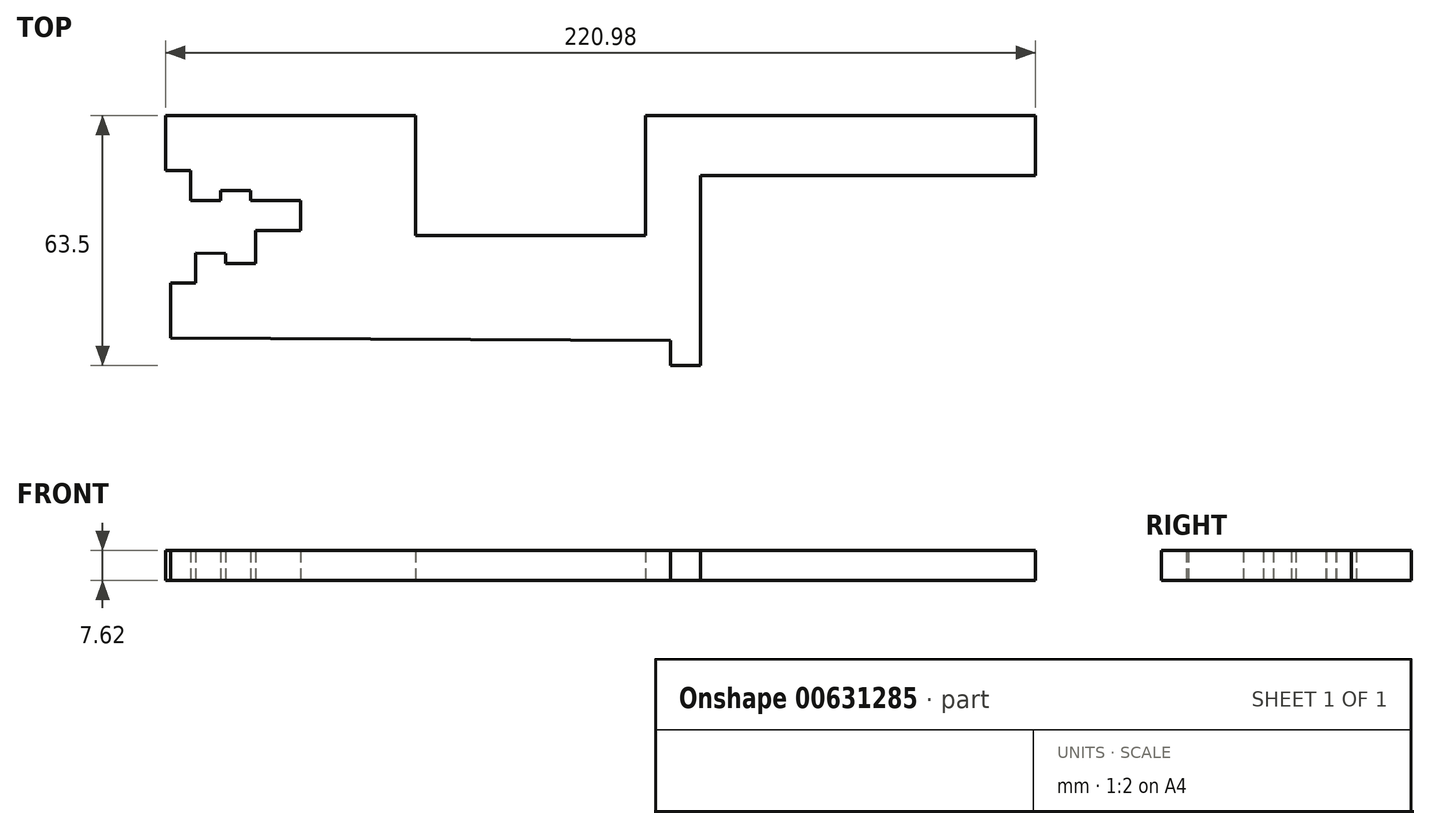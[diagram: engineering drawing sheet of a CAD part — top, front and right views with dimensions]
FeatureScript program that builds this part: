
annotation { "Feature Type Name" : "Feature", "Feature Type Description" : "" }
export const myFeature = defineFeature(function(context is Context, id is Id, definition is map)
    precondition{}
    {
        {
            var Q0;
            Q0=qCreatedBy(makeId("Top.planeOp"),FACE);
            var sketch = newSketch(context, id + "F0", { "sketchPlane" : qUnion([Q0])});
            skLineSegment(sketch, "E0", {"start": v(-135.89, 56.59) * mm, "end": v(-72.39, 56.59) * mm});
            skLineSegment(sketch, "E1", {"start": v(-72.39, 56.59) * mm, "end": v(-72.39, 26.1) * mm});
            skLineSegment(sketch, "E2", {"start": v(-72.39, 26.1) * mm, "end": v(-13.97, 26.1) * mm});
            skLineSegment(sketch, "E3", {"start": v(-13.97, 26.1) * mm, "end": v(-13.97, 56.59) * mm});
            skLineSegment(sketch, "E4", {"start": v(-13.97, 56.59) * mm, "end": v(85.1, 56.59) * mm});
            skLineSegment(sketch, "E5", {"start": v(85.1, 56.59) * mm, "end": v(85.1, 41.35) * mm});
            skLineSegment(sketch, "E6", {"start": v(85.1, 41.35) * mm, "end": v(0, 41.35) * mm});
            skLineSegment(sketch, "E7", {"start": v(0, 41.35) * mm, "end": v(0, -6.91) * mm});
            skLineSegment(sketch, "E8", {"start": v(0, -6.91) * mm, "end": v(-7.62, -6.91) * mm});
            skLineSegment(sketch, "E9", {"start": v(-7.62, -6.91) * mm, "end": v(-7.62, -0.56) * mm});
            skLineSegment(sketch, "E10", {"start": v(-7.62, -0.56) * mm, "end": v(-134.62, 0) * mm});
            skLineSegment(sketch, "E11", {"start": v(-134.62, 0) * mm, "end": v(-134.62, 13.97) * mm});
            skLineSegment(sketch, "E12", {"start": v(-134.62, 13.97) * mm, "end": v(-128.27, 13.97) * mm});
            skLineSegment(sketch, "E13", {"start": v(-128.27, 13.97) * mm, "end": v(-128.27, 13.97) * mm});
            skLineSegment(sketch, "E14", {"start": v(-128.27, 13.97) * mm, "end": v(-128.23, 21.59) * mm});
            skLineSegment(sketch, "E15", {"start": v(-128.23, 21.59) * mm, "end": v(-120.62, 21.56) * mm});
            skLineSegment(sketch, "E16", {"start": v(-135.89, 56.59) * mm, "end": v(-135.89, 42.62) * mm});
            skLineSegment(sketch, "E17", {"start": v(-135.89, 42.62) * mm, "end": v(-129.54, 42.62) * mm});
            skLineSegment(sketch, "E18", {"start": v(-129.54, 42.62) * mm, "end": v(-129.54, 35) * mm});
            skLineSegment(sketch, "E19", {"start": v(-129.54, 35) * mm, "end": v(-121.92, 34.96) * mm});
            skLineSegment(sketch, "E20", {"start": v(-121.92, 34.96) * mm, "end": v(-121.9, 37.5) * mm});
            skLineSegment(sketch, "E21", {"start": v(-120.62, 21.56) * mm, "end": v(-120.62, 19.02) * mm});
            skLineSegment(sketch, "E22", {"start": v(-120.62, 19.02) * mm, "end": v(-113, 18.98) * mm});
            skLineSegment(sketch, "E23", {"start": v(-113, 18.98) * mm, "end": v(-113, 21.52) * mm});
            skLineSegment(sketch, "E24", {"start": v(-121.9, 37.5) * mm, "end": v(-114.29, 37.47) * mm});
            skLineSegment(sketch, "E25", {"start": v(-114.29, 37.47) * mm, "end": v(-114.29, 37.47) * mm});
            skLineSegment(sketch, "E26", {"start": v(-114.29, 37.47) * mm, "end": v(-114.29, 34.93) * mm});
            skLineSegment(sketch, "E27", {"start": v(-114.29, 34.93) * mm, "end": v(-101.59, 34.93) * mm});
            skLineSegment(sketch, "E28", {"start": v(-101.59, 34.93) * mm, "end": v(-101.59, 27.3) * mm});
            skLineSegment(sketch, "E29", {"start": v(-101.59, 27.3) * mm, "end": v(-113, 27.3) * mm});
            skLineSegment(sketch, "E30", {"start": v(-113, 27.3) * mm, "end": v(-113, 15.97) * mm});
            skSolve(sketch);
        }
        {
            var Q0;
            Q0 = qSketchRegion(id + "F0", true);
            extrude(context, id + "F1", {"entities" : qUnion([Q0]), "depth" : 7.62 * mm, "offsetDistance" : 25.4 * mm});
        }
    });
